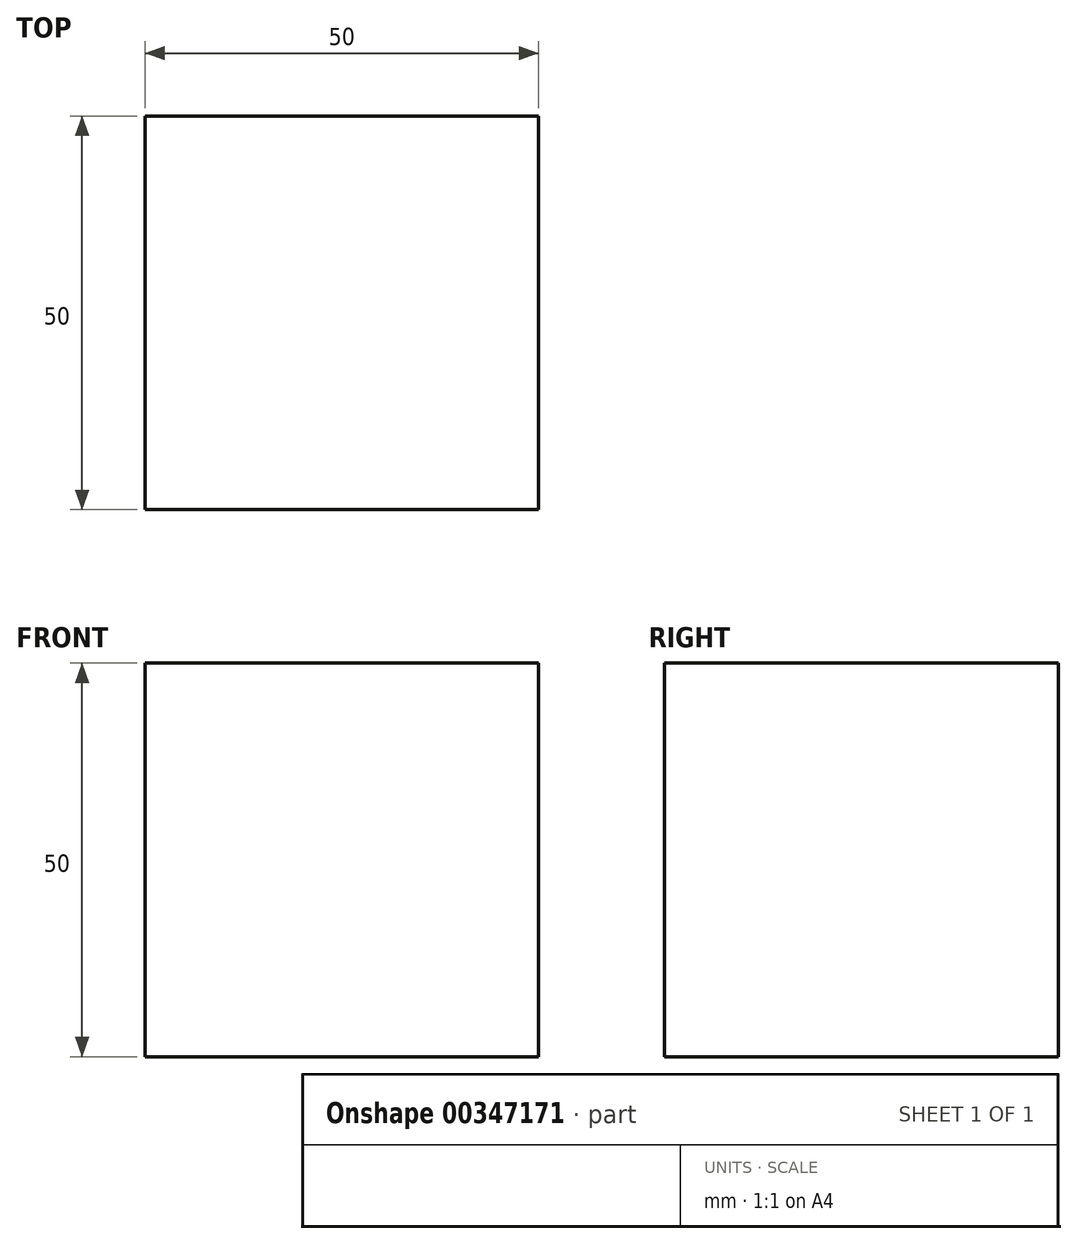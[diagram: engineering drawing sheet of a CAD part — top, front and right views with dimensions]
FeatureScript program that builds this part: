
annotation { "Feature Type Name" : "Feature", "Feature Type Description" : "" }
export const myFeature = defineFeature(function(context is Context, id is Id, definition is map)
    precondition{}
    {
        {
            var Q0;
            Q0=qCreatedBy(makeId("Top.planeOp"),FACE);
            var sketch = newSketch(context, id + "F0", { "sketchPlane" : qUnion([Q0])});
            skLineSegment(sketch, "E0.bottom", {"start": v(-23.05, 19.03) * mm, "end": v(26.95, 19.03) * mm});
            skLineSegment(sketch, "E0.top", {"start": v(-23.05, -30.97) * mm, "end": v(26.95, -30.97) * mm});
            skLineSegment(sketch, "E0.left", {"start": v(-23.05, 19.03) * mm, "end": v(-23.05, -30.97) * mm});
            skLineSegment(sketch, "E0.right", {"start": v(26.95, 19.03) * mm, "end": v(26.95, -30.97) * mm});
            skSolve(sketch);
        }
        {
            var Q0;
            Q0 = qSketchRegion(id + "F0", true);
            extrude(context, id + "F1", {"entities" : qUnion([Q0]), "depth" : 50 * mm});
        }
    });
